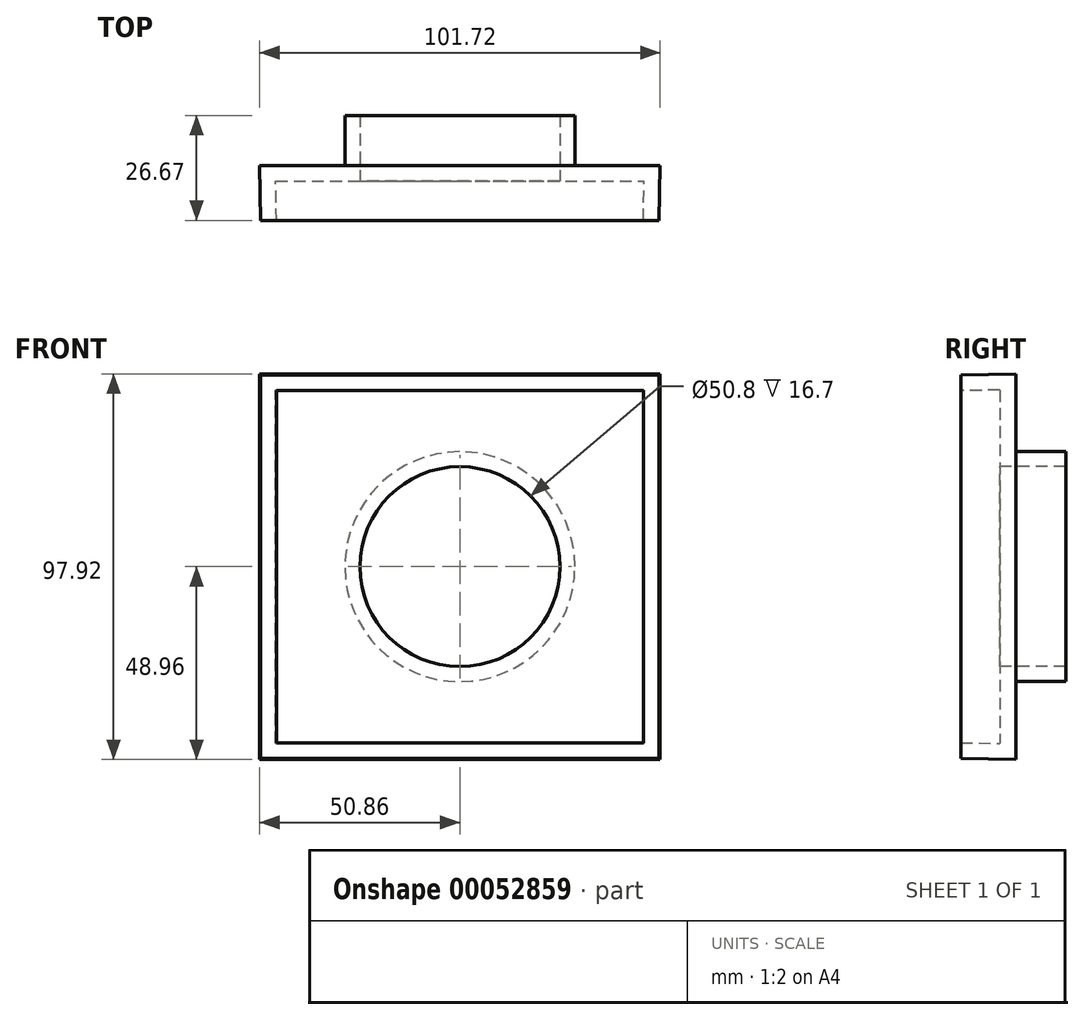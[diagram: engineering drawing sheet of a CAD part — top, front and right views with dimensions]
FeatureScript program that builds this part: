
annotation { "Feature Type Name" : "Feature", "Feature Type Description" : "" }
export const myFeature = defineFeature(function(context is Context, id is Id, definition is map)
    precondition{}
    {
        {
            var Q0;
            Q0=qCreatedBy(makeId("Front.planeOp"),FACE);
            var sketch = newSketch(context, id + "F0", { "sketchPlane" : qUnion([Q0])});
            skLineSegment(sketch, "E0.bottom", {"start": v(46.86, 44.96) * mm, "end": v(-46.86, 44.96) * mm});
            skLineSegment(sketch, "E0.top", {"start": v(46.86, -44.96) * mm, "end": v(-46.86, -44.96) * mm});
            skLineSegment(sketch, "E0.left", {"start": v(46.86, 44.96) * mm, "end": v(46.86, -44.96) * mm});
            skLineSegment(sketch, "E0.right", {"start": v(-46.86, 44.96) * mm, "end": v(-46.86, -44.96) * mm});
            skPoint(sketch, "E0.middle", {"position": v(0, 0) * mm});
            skLineSegment(sketch, "E1.bottom", {"start": v(50.86, 48.96) * mm, "end": v(-50.86, 48.96) * mm});
            skLineSegment(sketch, "E1.top", {"start": v(50.86, -48.96) * mm, "end": v(-50.86, -48.96) * mm});
            skLineSegment(sketch, "E1.left", {"start": v(50.86, 48.96) * mm, "end": v(50.86, -48.96) * mm});
            skLineSegment(sketch, "E1.right", {"start": v(-50.86, 48.96) * mm, "end": v(-50.86, -48.96) * mm});
            skSolve(sketch);
        }
        {
            var Q0;
            Q0=makeQuery(id+"F0.imprint","IMPRINT",FACE,{"disambiguationData":[TD([[makeQuery(id+"F0.imprint","IMPRINT",EDGE,{"derivedFrom":sQuery(id+"F0.wireOp",EDGE,"E0.bottom")}),-1.0]])]});
            var Q1;
            Q1=makeQuery(id+"F0.imprint","IMPRINT",FACE,{"disambiguationData":[TD([[makeQuery(id+"F0.imprint","IMPRINT",EDGE,{"derivedFrom":sQuery(id+"F0.wireOp",EDGE,"E0.bottom")}),1.0]])]});
            extrude(context, id + "F1", {"entities" : qUnion([Q0, Q1]), "depth" : 13.97 * mm, "hasDraft" : true, "draftAngle" : 1 * degree, "draftPullDirection" : true});
        }
        {
            var Q0;
            Q0=makeQuery(id+"F1.opExtrude","CAP_FACE",FACE,{"disambiguationData":[OSD([sQuery(id+"F0.wireOp",EDGE,"E1.bottom"),sQuery(id+"F0.wireOp",EDGE,"E1.top"),sQuery(id+"F0.wireOp",EDGE,"E1.left"),sQuery(id+"F0.wireOp",EDGE,"E1.right")])],"isStart":false});
            shell(context, id + "F2", {"entities" : qUnion([Q0]), "thickness" : 4 * mm});
        }
        {
            var Q0;
            Q0=makeQuery(id+"F1.opExtrude","CAP_FACE",FACE,{"disambiguationData":[OSD([sQuery(id+"F0.wireOp",EDGE,"E1.bottom"),sQuery(id+"F0.wireOp",EDGE,"E1.top"),sQuery(id+"F0.wireOp",EDGE,"E1.left"),sQuery(id+"F0.wireOp",EDGE,"E1.right")])],"isStart":true});
            var sketch = newSketch(context, id + "F3", { "sketchPlane" : qUnion([Q0])});
            skCircle(sketch, "E2", {"center": v(0, 0) * mm, "radius": 25.4 * mm});
            skCircle(sketch, "E3", {"center": v(0, 0) * mm, "radius": 29.21 * mm});
            skSolve(sketch);
        }
        {
            var Q0;
            Q0=makeQuery(id+"F3.imprint","IMPRINT",FACE,{"disambiguationData":[TD([[makeQuery(id+"F3.imprint","IMPRINT",EDGE,{"derivedFrom":sQuery(id+"F3.wireOp",EDGE,"E2")}),-1.0]])]});
            extrude(context, id + "F4", {"entities" : qUnion([Q0]), "operationType" : NewBodyOperationType.ADD, "depth" : 12.7 * mm});
        }
        {
            var Q0;
            Q0=makeQuery(id+"F4.boolean.opBoolean","SPLIT",FACE,{"disambiguationData":[TD([makeQuery(id+"F4.opExtrude","SWEPT_FACE",FACE,{"disambiguationData":[OSD([sQuery(id+"F3.wireOp",EDGE,"E2")])]})])],"derivedFrom":makeQuery(id+"F1.opExtrude","CAP_FACE",FACE,{"disambiguationData":[OSD([sQuery(id+"F0.wireOp",EDGE,"E1.bottom"),sQuery(id+"F0.wireOp",EDGE,"E1.top"),sQuery(id+"F0.wireOp",EDGE,"E1.left"),sQuery(id+"F0.wireOp",EDGE,"E1.right")])],"isStart":true})});
            extrude(context, id + "F5", {"entities" : qUnion([Q0]), "operationType" : NewBodyOperationType.REMOVE, "endBound" : BoundingType.UP_TO_NEXT, "oppositeDirection" : true, "depth" : 25.4 * mm});
        }
    });
